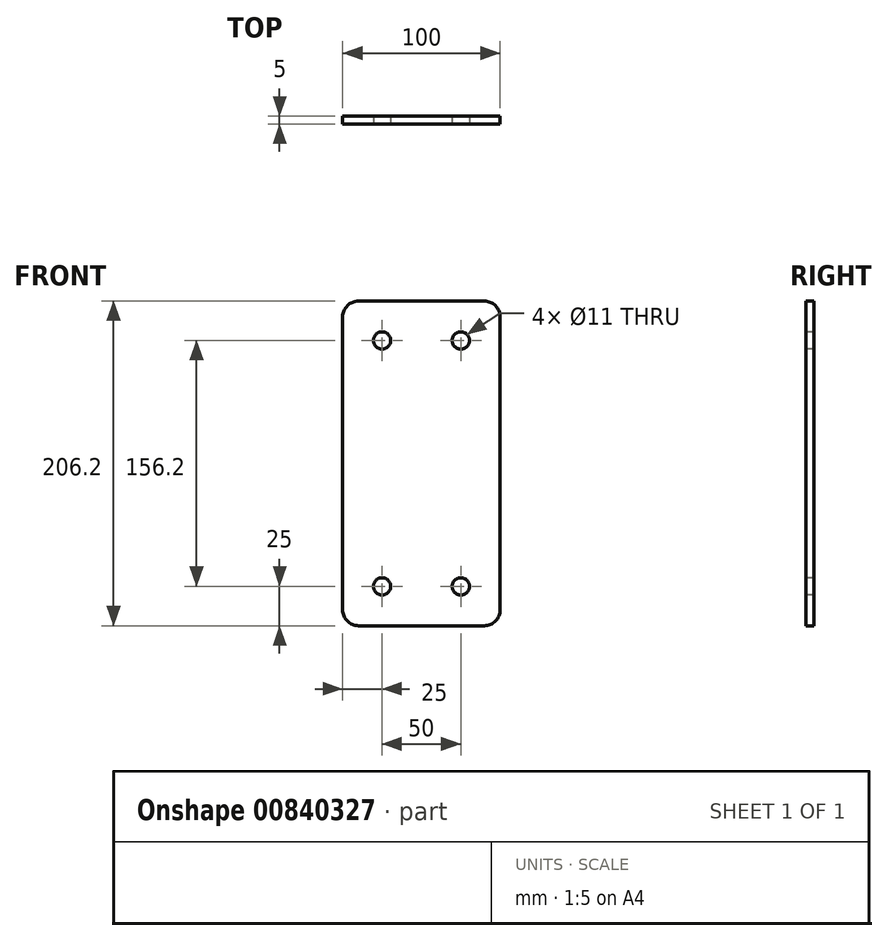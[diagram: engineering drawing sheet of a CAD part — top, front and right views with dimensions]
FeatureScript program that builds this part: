
annotation { "Feature Type Name" : "Feature", "Feature Type Description" : "" }
export const myFeature = defineFeature(function(context is Context, id is Id, definition is map)
    precondition{}
    {
        {
            var Q0;
            Q0=qCreatedBy(makeId("Front.planeOp"),FACE);
            var sketch = newSketch(context, id + "F0", { "sketchPlane" : qUnion([Q0])});
            skLineSegment(sketch, "E0.bottom", {"start": v(-40, 103.1) * mm, "end": v(40, 103.1) * mm});
            skLineSegment(sketch, "E0.top", {"start": v(-40, -103.1) * mm, "end": v(40, -103.1) * mm});
            skLineSegment(sketch, "E0.left", {"start": v(-50, 93.1) * mm, "end": v(-50, -93.1) * mm});
            skLineSegment(sketch, "E0.right", {"start": v(50, 93.1) * mm, "end": v(50, -93.1) * mm});
            skPoint(sketch, "E0.middle", {"position": v(0, 0) * mm});
            skPoint(sketch, "E1.visualSharp", {"position": v(-50, 103.1) * mm});
            skArc(sketch, "E1.filletArc", {"start": v(-40, 103.1) * mm, "mid": v(-47.07, 100.17) * mm, "end": v(-50, 93.1) * mm});
            skPoint(sketch, "E2.visualSharp", {"position": v(50, 103.1) * mm});
            skArc(sketch, "E2.filletArc", {"start": v(50, 93.1) * mm, "mid": v(47.07, 100.17) * mm, "end": v(40, 103.1) * mm});
            skPoint(sketch, "E3.visualSharp", {"position": v(50, -103.1) * mm});
            skArc(sketch, "E3.filletArc", {"start": v(40, -103.1) * mm, "mid": v(47.07, -100.17) * mm, "end": v(50, -93.1) * mm});
            skPoint(sketch, "E4.visualSharp", {"position": v(-50, -103.1) * mm});
            skArc(sketch, "E4.filletArc", {"start": v(-50, -93.1) * mm, "mid": v(-47.07, -100.17) * mm, "end": v(-40, -103.1) * mm});
            skSolve(sketch);
        }
        {
            var Q0;
            Q0 = qSketchRegion(id + "F0", true);
            extrude(context, id + "F1", {"entities" : qUnion([Q0]), "endBound" : BoundingType.SYMMETRIC, "depth" : 5 * mm, "offsetDistance" : 25 * mm});
        }
        {
            var Q0;
            Q0=makeQuery(id+"F1.opExtrude","CAP_FACE",FACE,{"disambiguationData":[OSD([sQuery(id+"F0.wireOp",EDGE,"E0.bottom"),sQuery(id+"F0.wireOp",EDGE,"E0.top"),sQuery(id+"F0.wireOp",EDGE,"E0.left"),sQuery(id+"F0.wireOp",EDGE,"E0.right"),sQuery(id+"F0.wireOp",EDGE,"E1.filletArc"),sQuery(id+"F0.wireOp",EDGE,"E2.filletArc"),sQuery(id+"F0.wireOp",EDGE,"E3.filletArc"),sQuery(id+"F0.wireOp",EDGE,"E4.filletArc")])],"isStart":false});
            var sketch = newSketch(context, id + "F2", { "sketchPlane" : qUnion([Q0])});
            skPoint(sketch, "E5", {"position": v(-25, 78.1) * mm});
            skPoint(sketch, "E6", {"position": v(25, 78.1) * mm});
            skPoint(sketch, "E7", {"position": v(25, -78.1) * mm});
            skPoint(sketch, "E8", {"position": v(-25, -78.1) * mm});
            skSolve(sketch);
        }
        {
            var Q0;
            Q0=sQuery(id+"F2.wireOp",VERTEX,"E5");
            var Q1;
            Q1=sQuery(id+"F2.wireOp",VERTEX,"E6");
            var Q2;
            Q2=sQuery(id+"F2.wireOp",VERTEX,"E7");
            var Q3;
            Q3=sQuery(id+"F2.wireOp",VERTEX,"E8");
            var Q4;
            Q4=makeQuery(id+"F1.opExtrude","SWEPT_BODY",BODY,{"disambiguationData":[OSD([sQuery(id+"F0.wireOp",EDGE,"E0.bottom"),sQuery(id+"F0.wireOp",EDGE,"E0.top"),sQuery(id+"F0.wireOp",EDGE,"E0.left"),sQuery(id+"F0.wireOp",EDGE,"E0.right"),sQuery(id+"F0.wireOp",EDGE,"E1.filletArc"),sQuery(id+"F0.wireOp",EDGE,"E2.filletArc"),sQuery(id+"F0.wireOp",EDGE,"E3.filletArc"),sQuery(id+"F0.wireOp",EDGE,"E4.filletArc")])]});
            hole(context, id + "F3", {"style" : HoleStyle.SIMPLE, "endStyle" : HoleEndStyle.BLIND, "standardTappedOrClearance" : lookupTablePath({ "fit" : "Normal", "standard" : "ISO", "size" : "M10", "type" : "Clearance" }), "standardBlindInLast" : lookupTablePath({ "fit" : "Standard", "standard" : "ISO", "size" : "M10", "type" : "Clearance" }), "holeDiameter" : 11 * mm, "majorDiameter" : 10 * mm, "holeDepth" : 24.5 * mm, "isTappedThrough" : true, "tappedDepth" : 20 * mm, "tapClearance" : 3, "startFromSketch" : true, "locations" : qUnion([Q0, Q1, Q2, Q3]), "scope" : qUnion([Q4])});
        }
    });
